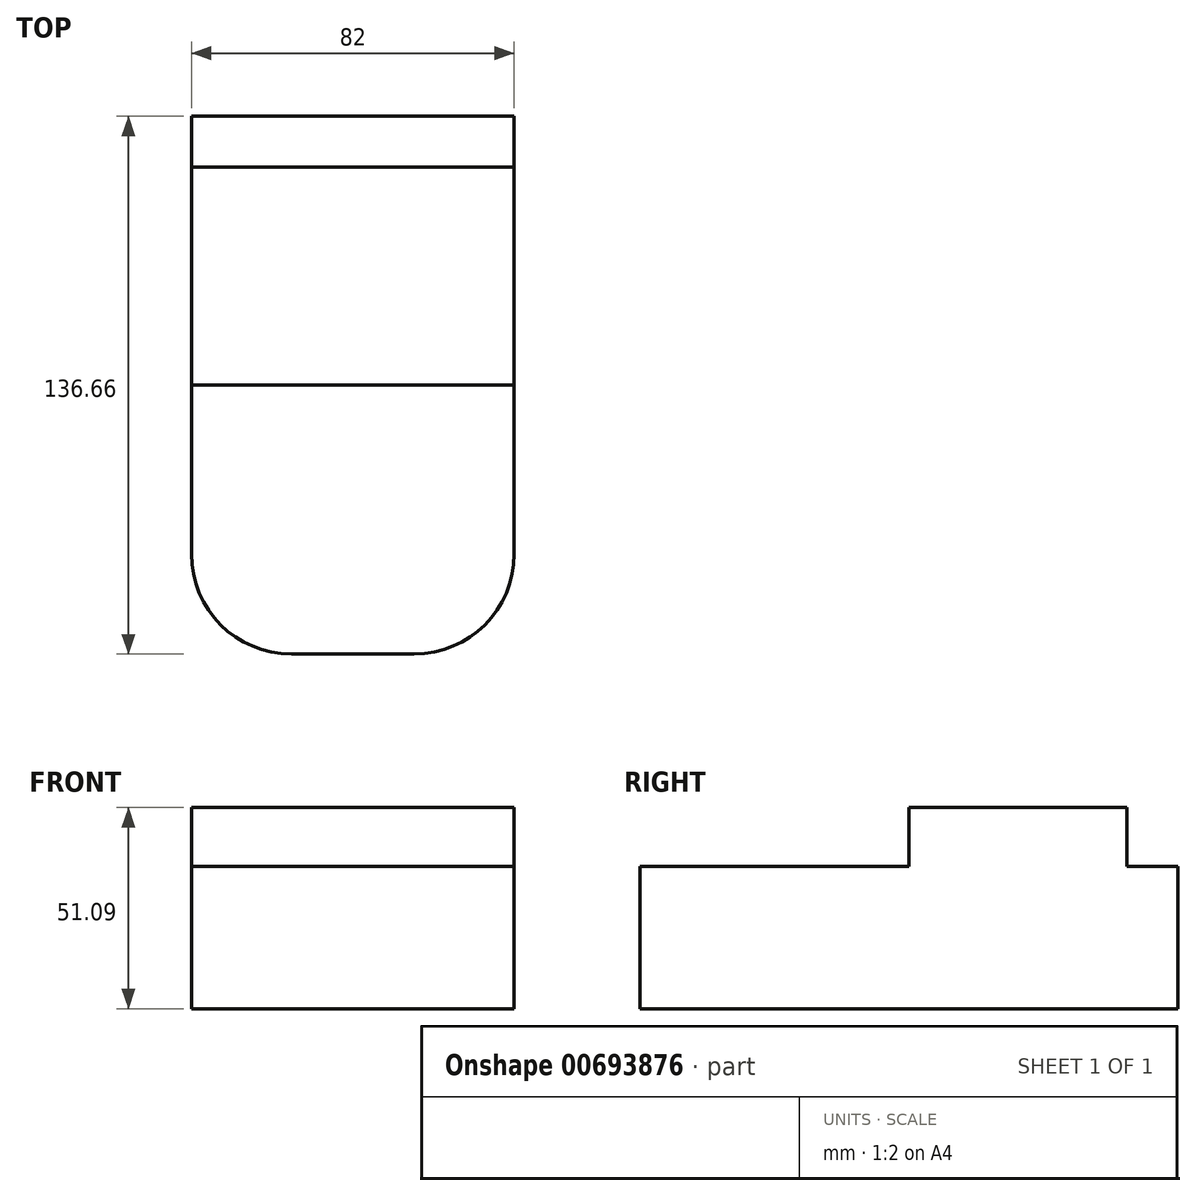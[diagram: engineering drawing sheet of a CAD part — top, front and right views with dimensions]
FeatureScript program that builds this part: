
annotation { "Feature Type Name" : "Feature", "Feature Type Description" : "" }
export const myFeature = defineFeature(function(context is Context, id is Id, definition is map)
    precondition{}
    {
        {
            var Q0;
            Q0=qCreatedBy(makeId("Top.planeOp"),FACE);
            var sketch = newSketch(context, id + "F0", { "sketchPlane" : qUnion([Q0])});
            skLineSegment(sketch, "E0.bottom", {"start": v(15.6, -68.33) * mm, "end": v(-15.6, -68.33) * mm});
            skLineSegment(sketch, "E0.top", {"start": v(41, 68.33) * mm, "end": v(-41, 68.33) * mm});
            skLineSegment(sketch, "E0.left", {"start": v(41, -42.93) * mm, "end": v(41, 68.33) * mm});
            skLineSegment(sketch, "E0.right", {"start": v(-41, -42.93) * mm, "end": v(-41, 68.33) * mm});
            skPoint(sketch, "E0.middle", {"position": v(0, 0) * mm});
            skPoint(sketch, "E1.visualSharp", {"position": v(-41, -68.33) * mm});
            skArc(sketch, "E1.filletArc", {"start": v(-41, -42.93) * mm, "mid": v(-33.56, -60.89) * mm, "end": v(-15.6, -68.33) * mm});
            skPoint(sketch, "E2.visualSharp", {"position": v(41, -68.33) * mm});
            skArc(sketch, "E2.filletArc", {"start": v(15.6, -68.33) * mm, "mid": v(33.56, -60.89) * mm, "end": v(41, -42.93) * mm});
            skSolve(sketch);
        }
        {
            var Q0;
            Q0=qSketchRegion(id+"F0",true);
            extrude(context, id + "F1", {"entities" : qUnion([Q0]), "depth" : 36.17 * mm, "offsetDistance" : 25.4 * mm});
        }
        {
            var Q0;
            Q0=makeQuery(id+"F1.opExtrude","CAP_FACE",FACE,{"disambiguationData":[OSD([sQuery(id+"F0.wireOp",EDGE,"E0.bottom"),sQuery(id+"F0.wireOp",EDGE,"E0.top"),sQuery(id+"F0.wireOp",EDGE,"E0.left"),sQuery(id+"F0.wireOp",EDGE,"E0.right"),sQuery(id+"F0.wireOp",EDGE,"E1.filletArc"),sQuery(id+"F0.wireOp",EDGE,"E2.filletArc")])],"isStart":false});
            var sketch = newSketch(context, id + "F2", { "sketchPlane" : qUnion([Q0])});
            skLineSegment(sketch, "E3", {"start": v(-41, 55.35) * mm, "end": v(41, 55.35) * mm});
            skLineSegment(sketch, "E4", {"start": v(-41, 0) * mm, "end": v(41, 0) * mm});
            skLineSegment(sketch, "E5", {"start": v(-41, 0) * mm, "end": v(-41, 55.35) * mm});
            skLineSegment(sketch, "E6", {"start": v(41, 0) * mm, "end": v(41, 55.35) * mm});
            skSolve(sketch);
        }
        {
            var Q0;
            Q0=qSketchRegion(id+"F2",true);
            extrude(context, id + "F3", {"entities" : qUnion([Q0]), "operationType" : NewBodyOperationType.ADD, "depth" : 14.92 * mm, "offsetDistance" : 25.4 * mm});
        }
    });
